# Revit family: Piezo_Button_Valve-Acorn-Master-Trol-Plus-MTPP2-MA2
name_source: partatom
category: Mechanical Equipment
units: mm (PartAtom-declared; Revit-internal decimal feet)

## family parameters
Classification = None
Cut with Voids When Loaded = No
Host = Face
OmniClass Number = 23.65.55.14.17
OmniClass Title = Adjusting/Controlling Valves for Liquid Services
Part Type = Normal
Room Calculation Point = No
Round Connector Dimension = Use Diameter
Shared = Yes

## types (1)
- MTPP2-MA2
    ADA Compliant = Yes
    Assembly Code = D2090900
    CW Connection = Yes
    CWFU = 0
    Default Elevation = 0 "
    Depth Of Body = 5.518 "
    Description = Option: Master-Trol® Plus Hot & Cold Piezo Button Valve
    Finish = Stainless Steel-Acorn-Satin
    HW Connection = Yes
    HWFU = 0
    IAPMO Compliance = Valve conforms with the lead free requirements of NSF61, Section 9, 1997; Federal Public Law 111-380 and ADA requirements.
    Inlet Diameter Connection = 0.5 "
    Installation Type = Surface Mounted
    Length = 8.256 "
    Manufacturer = Acorn Engineering
    Material = Stainless Steel-Acorn-Satin
    Max. Working Pressure = 100 Pounds per Square Inch (689.5 Kilopascal)
    Maximum Temperature = 130º F (54º C)
    Min. Working Pressure = 30 Pounds per Square Inch (206.8 Kilopascal)
    Model = MTPP2-MA2
    Product Documentation Link = https://www.acorneng.com
    Product Page URL = https://www.acorneng.com
    URL = https://www.acorneng.com
    Vent Connection = No
    WFU = 0
    Waste Connection = No
    Width = 8.25 "

## geometry (parser evidence)
native form markers: Sweep x3
no freeform markers — native parametric forms only
